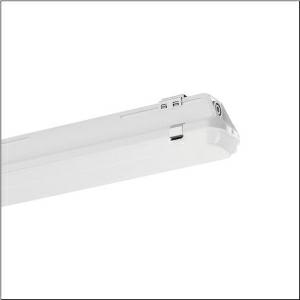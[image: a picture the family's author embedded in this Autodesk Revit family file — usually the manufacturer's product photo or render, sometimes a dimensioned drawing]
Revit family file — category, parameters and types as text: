
# Revit family: monsun_11_51fp109p460h
name_source: partatom
category: Lighting Fixtures
units: mm (PartAtom-declared; Revit-internal decimal feet)

## family parameters
Cut with Voids When Loaded = No
Host = Face
Light Source = No
Part Type = Normal
Room Calculation Point = No
Round Connector Dimension = Use Diameter
Shared = No

## types (1)
- Monsun 11 (1 x LED, 6100 lm, 34 W, 4000K)
    Apparent Load = 34 VA
    CIE Flux Codes = 47 77 93 94 100
    Color Rendering = 80
    Color Temperature = 4000K
    Default Elevation = 1800 mm
    Description = Monsun 11, damp-proof luminaire, chain hanger, primary optical cover: enclosure, of PMMA, light emission: direct distribution, primary light characteristic: symmetric, installation type: suspended mounting, surface-mounted, horizontal mounting, vertical mounting, LED, rated luminous flux: 6.100lm, luminous efficacy: 179lm/W, light colour: 840, colour temperature: 4000K, control gear: ON/OFF, CLOi, with terminal, 3-pole, max. 2.5mm², mains connection: 220..240V, AC, 50/60Hz, start of lifetime: 34W, end of service life: 38W, luminaire housing, of glass-fibre reinforced polyester, uncoated, bright grey, incl. chain hanger, length: 1.590mm, width: 90mm, height: 88mm, clip for enclosure, of stainless steel (V2A), ceiling mounting element, of stainless steel (V2A), chain hanger, of stainless steel (V2A), protection rating (complete): IP66, insulation class (complete): insulation class I (protective earthing), certification: CE, ENEC, VDE, UKCA, protection symbol: D, impact resistance: IK04, permissible operating ambient temperature: -35..+40°C, standard: EN 50419, EN 60598-2-1, no direct snow, no direct sun, no direct rain, for indoor or canopied outdoor use, corresponds to IFS (International Featured Standards) requirements for safety and quality in the food industry, contact your sales advisor before using the luminaires in applications with unclear chemical exposure, large temperature fluctuations or condensation-forming humidity, LABS conformity tested according to VDMA 24364:2018-05, packaging unit: 1 piece
    Height = 89 mm
    Lamp = 1 x LED
    Lamp Light Flux = 6100 lm
    Lamp Power = 34 W
    Lamp count = 1
    Length = 1590 mm
    Luminous efficacy = 179 lm/W
    Manufacturer = Siteco
    ModVariant = No
    Model = 51FP109P460H
    Mounting Place = Ceiling
    Mounting Type = Surface mounted
    Number of Poles = 1
    OnlyDefault = Yes
    Power Factor = 1
    Product Name = Monsun 11
    Product group = damp-proof luminaire
    ProductGroupID = 300
    Protection Class = Protection class I
    Protection Degree = IP 66
    RLX_Detail_Level = 1
    RLX_Emergency_Light_Flux = 0 lm
    RLX_Emergency_Type = 0
    RLX_Emergency_Type_DB = No
    RlxData = <blob elided: 88481 chars, md5=599de49a>
    Socket = socket
    Standby Power = 0 W
    System Light Flux = 6100 lm
    System Power = 34 W
    Type Comments = Product without accessories
    Type Image = l_1349237.jpg
    URL = http://relux.com
    VarID = ---
    Voltage = 0 V
    Weight = 0.00 kg
    Width = 90 mm

## geometry (parser evidence)
native form markers: Blend x4, Sweep x13
no freeform markers — native parametric forms only
